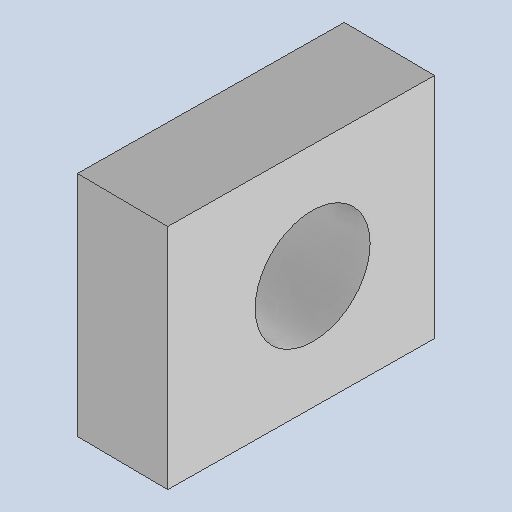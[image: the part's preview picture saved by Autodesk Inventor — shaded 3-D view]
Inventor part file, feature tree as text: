
AUTODESK INVENTOR PART (.ipt)
format: ipt  version: 2025 (Build 290162010, 162A)  size: 151,040 bytes
history: native  units: mm
features: other x4, sketch x3, extrude x2, hole x1, reference x1, projected_geometry x1
ambient origin geometry x8: Origin, YZ Plane, XZ Plane, XY Plane, X Axis, Y Axis, Z Axis, Center Point
bodies: Volumenkörper1 (feature_tree)
feature tree (12):
  extrude  "Extrusion1"  TaperAngle=0.0deg  [1 undecoded]
  extrude  "Extrusion2"  Depth=1.0mm
  hole  "Bohrung1"  [1 undecoded]
  sketch  "Skizze1"  dims[d0=10.0mm d1=0.0mm d2=0.0mm d3=0.0mm]
  reference  "Referenz2"
  sketch  "Skizze2"  dims[d4=5.0mm d5=6.0mm d6=5.0mm d7=2.0mm d8=90.0deg d9=8.0mm d10=20.594885mm d11=1.0mm]
  projected_geometry  "Projizierte Kontur1"
  sketch  "Skizze3"
  other  "<userpath>\GIT\HDVKBM\CAD\Krandemonstrator\Demonstrator.iam"
  other  "Demonstrator.iam"
  other  "UmlenkrolleHalterEinfachAngle:1"
  other  "HalterUmlenkrolleOVL:1"
note: 2 required parameter values undecoded (feature->parameter linkage not recoverable at this tier; creation-order binding heuristic only, values carry confidence <= 0.55)
